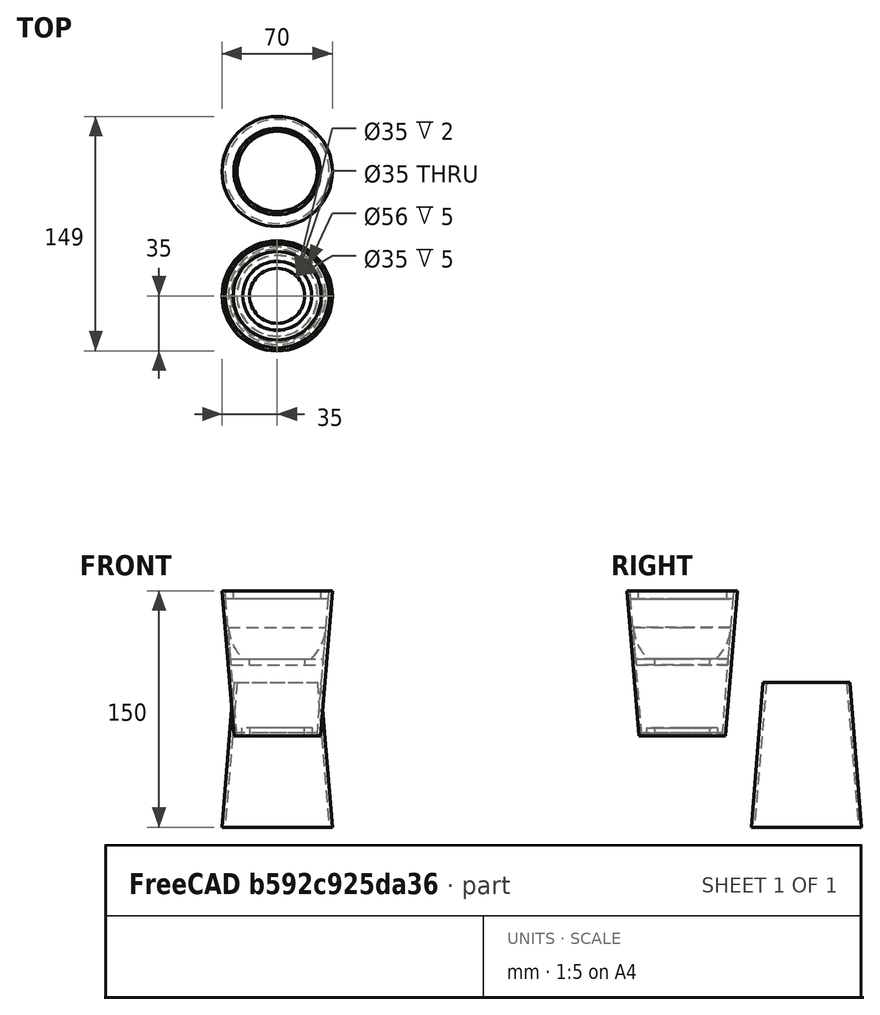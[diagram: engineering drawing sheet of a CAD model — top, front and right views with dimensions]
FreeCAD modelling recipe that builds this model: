
FCSTD DOCUMENT  (FreeCAD 1.0R39109 (Git))
Label: NojkaAA
License: All rights reserved
LicenseURL: https://en.wikipedia.org/wiki/All_rights_reserved
objects: Part::Cylinder×12, Part::Cut×12, Part::Cone×10, PartDesign::Body×6, PartDesign::ShapeBinder×5, Part::Mirroring×3, Part::Sphere×2, App::Part×2, Sketcher::SketchObject×1
note: 52 computed .brp shape members not serialized (recipe doc carries the construction recipe); baked Part::Feature solids carry a one-line shape summary decoded from their .brp

FEATURE [Part::Cone] Cone
  Angle = 360
  AttacherType = Attacher::AttachEngine3D
  Height = 92
  Radius1 = 27.5
  Radius2 = 35
FEATURE [Part::Cone] Cone001
  Angle = 360
  AttacherType = Attacher::AttachEngine3D
  Height = 92
  Radius1 = 25.5
  Radius2 = 33
FEATURE [Part::Cylinder] Cylinder
  Angle = 360
  AttacherType = Attacher::AttachEngine3D
  FirstAngle = 0
  Height = 4
  Placement = pos=(0,0,45) rot=(0,0,1;0rad)
  Radius = 29.17
  SecondAngle = 0
FEATURE [Part::Cylinder] Cylinder001
  Angle = 360
  AttacherType = Attacher::AttachEngine3D
  FirstAngle = 0
  Height = 4
  Placement = pos=(0,0,45) rot=(0,0,1;0rad)
  Radius = 17.5
  SecondAngle = 0
FEATURE [PartDesign::ShapeBinder] CopyCut
  TraceSupport = false
FEATURE [PartDesign::ShapeBinder] CopyCylinder002
  Placement = pos=(0,0,57) rot=(0,0,1;0rad)
  TraceSupport = false
FEATURE [PartDesign::ShapeBinder] CopyCut001
  Placement = pos=(0,0,45) rot=(0,0,1;0rad)
  TraceSupport = false
FEATURE [PartDesign::Body] Body
  AllowCompound = false
  Group = -> [CopyCut,CopyCylinder002,CopyCut001]
  Origin = -> Origin
FEATURE [PartDesign::ShapeBinder] CopyCut002
  Placement = pos=(0,0,45) rot=(0,0,1;0rad)
  TraceSupport = false
FEATURE [PartDesign::ShapeBinder] CopyCut003
  TraceSupport = false
FEATURE [PartDesign::Body] Body001
  AllowCompound = false
  Group = -> [CopyCut003]
  Origin = -> Origin001
FEATURE [Part::Cone] Cone002
  Angle = 360
  AttacherType = Attacher::AttachEngine3D
  Height = 20
  Placement = pos=(0,0,49) rot=(0,0,1;0rad)
  Radius1 = 29.5
  Radius2 = 31
FEATURE [Part::Sphere] Sphere
  Angle1 = -90
  Angle2 = 90
  Angle3 = 360
  AttacherType = Attacher::AttachEngine3D
  Placement = pos=(0,0,71) rot=(0,0,1;0rad)
  Radius = 31
FEATURE [Part::Cut] Cut
  Base = -> Cone
  Tool = -> Cone001
FEATURE [Part::Cut] Cut001
  Base = -> Cylinder
  Tool = -> Cylinder001
FEATURE [Sketcher::SketchObject] Sketch
  ArcFitTolerance = 0
  FullyConstrained = true
  MakeInternals = false
  Placement = pos=(30.12,0,57) rot=(0,0,1;0rad)
FEATURE [Part::Mirroring] Part__Mirroring  label="Cut (Mirror #1)"
  Base = (0,0,0)
  Normal = (1,0,0)
  Placement = pos=(0,79,34) rot=(1,0,0;3.14159rad)
  Source = -> Cut
FEATURE [Part::Mirroring] Part__Mirroring001  label="Cut001 (Mirror #2)"
  Base = (0,0,0)
  Normal = (1,0,0)
  Source = -> Cut001
FEATURE [PartDesign::Body] Body002
  AllowCompound = false
  Origin = -> Origin002
FEATURE [Part::Cone] Cone003
  Angle = 360
  AttacherType = Attacher::AttachEngine3D
  Height = 2
  Radius1 = 25.5
  Radius2 = 25.7
FEATURE [Part::Cylinder] Cylinder003
  Angle = 360
  AttacherType = Attacher::AttachEngine3D
  FirstAngle = 0
  Height = 10
  Radius = 17.5
  SecondAngle = 0
FEATURE [Part::Cut] Cut003
  Base = -> Cone003
  Tool = -> Cylinder003
FEATURE [Part::Cone] Cone004
  Angle = 360
  AttacherType = Attacher::AttachEngine3D
  Height = 5
  Placement = pos=(0,0,87) rot=(0,0,1;0rad)
  Radius1 = 32.6
  Radius2 = 33
FEATURE [Part::Cylinder] Cylinder004
  Angle = 360
  AttacherType = Attacher::AttachEngine3D
  FirstAngle = 0
  Height = 10
  Placement = pos=(0,0,86) rot=(0,0,1;0rad)
  Radius = 28
  SecondAngle = 0
FEATURE [Part::Cut] Cut002
  Base = -> Cone002
  Tool = -> Sphere
FEATURE [Part::Mirroring] Part__Mirroring002  label="Cut002 (Mirror #3)"
  Base = (0,0,0)
  Normal = (1,0,0)
  Source = -> Cut002
FEATURE [Part::Cut] Cut004
  Base = -> Cone004
  Tool = -> Cylinder004
FEATURE [Part::Cylinder] Cylinder005
  Angle = 360
  AttacherType = Attacher::AttachEngine3D
  FirstAngle = 0
  Height = 5
  Radius = 22.5
  SecondAngle = 0
FEATURE [Part::Cylinder] Cylinder006
  Angle = 360
  AttacherType = Attacher::AttachEngine3D
  FirstAngle = 0
  Height = 10
  Radius = 17.5
  SecondAngle = 0
FEATURE [Part::Cut] Cut005
  Base = -> Cylinder005
  Tool = -> Cylinder006
FEATURE [App::Part] Part  label="v1"
  Group = -> [Body,Body001,CopyCut002,Sketch,Cone,Cone001,Cut,Part__Mirroring,Cylinder,Cylinder001,Cut001,Part__Mirroring001,Cone002,Sphere,Cut002,Part__Mirroring002,Body002,Cone003,Cylinder003,Cut003,Cone004,Cylinder004,Cut004,Cylinder005,Cylinder006,Cut005]
  Origin = -> Origin003
FEATURE [PartDesign::Body] Body003
  AllowCompound = false
  Origin = -> Origin004
FEATURE [PartDesign::Body] Body005
  AllowCompound = false
  Origin = -> Origin006
FEATURE [Part::Cone] Cone005
  Angle = 360
  AttacherType = Attacher::AttachEngine3D
  Height = 92
  Radius1 = 27.5
  Radius2 = 35
FEATURE [Part::Cone] Cone006
  Angle = 360
  AttacherType = Attacher::AttachEngine3D
  Height = 92
  Radius1 = 25.5
  Radius2 = 33
FEATURE [Part::Cone] Cone007
  Angle = 360
  AttacherType = Attacher::AttachEngine3D
  Height = 20
  Placement = pos=(0,0,49) rot=(0,0,1;0rad)
  Radius1 = 29.5
  Radius2 = 31
FEATURE [Part::Cone] Cone008
  Angle = 360
  AttacherType = Attacher::AttachEngine3D
  Height = 2
  Radius1 = 25.5
  Radius2 = 25.7
FEATURE [Part::Cone] Cone009
  Angle = 360
  AttacherType = Attacher::AttachEngine3D
  Height = 5
  Placement = pos=(0,0,87) rot=(0,0,1;0rad)
  Radius1 = 32.6
  Radius2 = 33
FEATURE [Part::Cut] Cut006
  Base = -> Cone005
  Tool = -> Cone006
FEATURE [Part::Cylinder] Cylinder007
  Angle = 360
  AttacherType = Attacher::AttachEngine3D
  FirstAngle = 0
  Height = 4
  Placement = pos=(0,0,45) rot=(0,0,1;0rad)
  Radius = 29.17
  SecondAngle = 0
FEATURE [Part::Cylinder] Cylinder008
  Angle = 360
  AttacherType = Attacher::AttachEngine3D
  FirstAngle = 0
  Height = 4
  Placement = pos=(0,0,45) rot=(0,0,1;0rad)
  Radius = 17.5
  SecondAngle = 0
FEATURE [Part::Cut] Cut007
  Base = -> Cylinder007
  Tool = -> Cylinder008
FEATURE [Part::Cylinder] Cylinder009
  Angle = 360
  AttacherType = Attacher::AttachEngine3D
  FirstAngle = 0
  Height = 10
  Radius = 17.5
  SecondAngle = 0
FEATURE [Part::Cut] Cut009
  Base = -> Cone008
  Tool = -> Cylinder009
FEATURE [Part::Cylinder] Cylinder010
  Angle = 360
  AttacherType = Attacher::AttachEngine3D
  FirstAngle = 0
  Height = 10
  Placement = pos=(0,0,86) rot=(0,0,1;0rad)
  Radius = 28
  SecondAngle = 0
FEATURE [Part::Cut] Cut010
  Base = -> Cone009
  Tool = -> Cylinder010
FEATURE [Part::Cylinder] Cylinder011
  Angle = 360
  AttacherType = Attacher::AttachEngine3D
  FirstAngle = 0
  Height = 5
  Radius = 22.5
  SecondAngle = 0
FEATURE [Part::Cylinder] Cylinder012
  Angle = 360
  AttacherType = Attacher::AttachEngine3D
  FirstAngle = 0
  Height = 10
  Radius = 17.5
  SecondAngle = 0
FEATURE [Part::Cut] Cut011
  Base = -> Cylinder011
  Tool = -> Cylinder012
FEATURE [Part::Sphere] Sphere001
  Angle1 = -90
  Angle2 = 90
  Angle3 = 360
  AttacherType = Attacher::AttachEngine3D
  Placement = pos=(0,0,71) rot=(0,0,1;0rad)
  Radius = 31
FEATURE [Part::Cut] Cut008
  Base = -> Cone007
  Tool = -> Sphere001
FEATURE [PartDesign::Body] Body004
  AllowCompound = false
  Group = -> [Cut008]
  Origin = -> Origin005
FEATURE [App::Part] Part001  label="v2"
  Group = -> [Cone006,Cone005,Cut006,Cylinder007,Cylinder008,Cut007,Body003,Body004,Body005,Cone008,Cylinder009,Cut009,Cone009,Cylinder010,Cut010,Cylinder011,Cylinder012,Cut011]
  Origin = -> Origin007
